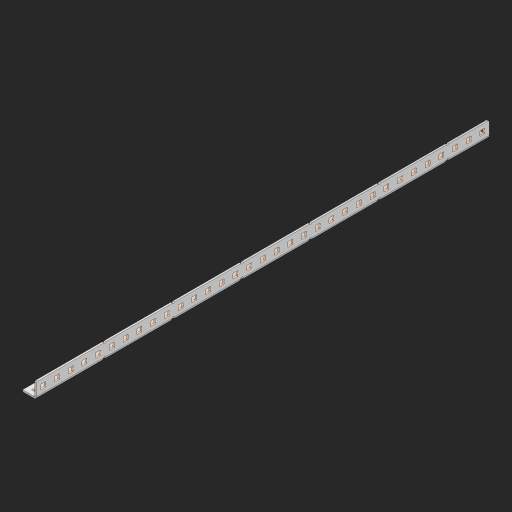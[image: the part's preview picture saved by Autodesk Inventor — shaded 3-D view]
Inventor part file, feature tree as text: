
AUTODESK INVENTOR PART (.ipt)
format: ipt  version: 2023 (Build 270158000, 158)  size: 1,024,000 bytes
history: native  units: in
note: dims shown in document units (in); Inventor stores cm internally (conversion verified against a paired STEP export)
features: other x71, extrude x65, sheet_metal_op x10, sketch x8, mirror x1, pattern_linear x1, chamfer x1
ambient origin geometry x8: Origin, YZ Plane, XZ Plane, XY Plane, X Axis, Y Axis, Z Axis, Center Point
bodies: Solid1 (feature_tree), Body (feature_tree)
feature tree (157):
  other  "Flange Pattern Plane"
  sheet_metal_op  "Flange Pattern"
  sheet_metal_op  "Body Pattern"
  other  "Arc Length"
  mirror  "Notch Mirror"
  pattern_linear  "Notch Pattern"  Spacing1=0.25in  [1 undecoded]
  chamfer  "End Chamfer"
  extrude  "Half Cut"  Depth=0.0625in
  sketch  "Sketch1"  dims[d0=1.5in]
  other  "Plate1"
  sketch  "Sketch2"  dims[d1=16.5in]
  other  "Plate2"
  sheet_metal_op  "Bend1"
  sheet_metal_op  "Corner1"
  sketch  "Sketch3"  dims[d2=0.0625in]
  other  "Flange Pattern Sketch"
  sketch  "Sketch7"  dims[d3=0.0625in]
  other  "Srf1"
  other  "Srf2"
  sketch  "Sketch8"  dims[d4=0.0312in]
  sketch  "Sketch9"  dims[d5=0.125in]
  other  "Srf91"
  sheet_metal_op  "Body Pattern Sketch"
  other  "Srf92"
  sketch  "Sketch13"  dims[d6=0.0625in]
  sketch  "Sketch14"  dims[d7=0.5in d8=90.0deg d9=0.0312in d10=0.25in d11=0.0625in d12=0.0625in d16=0.182in d17=0.02in d18=0.0625in d19=0.0in d20=0.25in d21=0.25in d46=0.172in d47=1.0in d48=0.0in d49=0.182in d50=0.02in d51=0.25in d52=0.25in d53=0.0625in d54=0.0in d55=0.172in d56=1.0in d57=0.0in d60=12.9921in d62=0.5in d63=0.3937in d65=0.5in d85=0.1473in d86=0.1782in d88=0.04in d89=0.0625in d90=0.0in d91=0.04in d92=0.0491in d95=2.5in d96=0.04in d97=0.25in d98=45.0deg d101=0.0in d102=2.497in d131=0.5in d132=12.9921in d134=0.5in d139=0.5in]
  other  "Srf856"
  other  "Srf1310"
  other  "Srf1311"
  other  "Srf1312"
  other  "Srf1376"
  other  "Srf1377"
  other  "Srf1728"
  other  "Srf1755"
  other  "Srf1878"
  other  "Srf1879"
  other  "Srf1880"
  other  "Srf1881"
  other  "Srf1882"
  other  "Srf1883"
  other  "Srf1884"
  other  "Srf1885"
  other  "Srf1886"
  other  "Srf1887"
  other  "Srf1888"
  other  "Srf1889"
  other  "Srf1890"
  other  "Srf1891"
  other  "Srf1892"
  other  "Srf1893"
  other  "Srf1894"
  other  "Srf1895"
  other  "Srf1896"
  other  "Srf1897"
  other  "Srf1898"
  other  "Srf1899"
  other  "Srf1900"
  other  "Srf1901"
  other  "Srf1902"
  other  "Srf1903"
  other  "Srf1904"
  other  "Srf1942"
  other  "Srf1943"
  other  "Srf1944"
  other  "Srf1945"
  other  "Srf1946"
  other  "Srf1947"
  other  "Srf1948"
  other  "Srf1949"
  other  "Srf1950"
  other  "Srf1951"
  other  "Srf1952"
  other  "Srf1953"
  other  "Srf1954"
  other  "Srf1955"
  other  "Srf1956"
  other  "Srf1957"
  other  "Srf1958"
  other  "Srf1959"
  other  "Srf1960"
  other  "Srf1961"
  other  "Srf1962"
  other  "Srf1963"
  other  "Srf1964"
  other  "Srf1965"
  other  "Srf1966"
  other  "Srf1967"
  other  "Srf1968"
  sheet_metal_op  "Flange Stamp"
  sheet_metal_op  "Flange Circle"
  sheet_metal_op  "Body Stamp"
  sheet_metal_op  "Body Circle"
  sheet_metal_op  "Notch"
  extrude  "ExtrusionSrf2"  Depth=0.0625in
  extrude  "ExtrusionSrf92"  Depth=0.5in
  extrude  "ExtrusionSrf856"  Depth=0.02in
  extrude  "ExtrusionSrf1310"  Depth=0.0625in
  extrude  "ExtrusionSrf1311"  TaperAngle=0.0deg  [1 undecoded]
  extrude  "ExtrusionSrf1312"  Depth=0.5in
  extrude  "ExtrusionSrf1376"  Depth=0.5in
  extrude  "ExtrusionSrf1377"  Depth=0.5in
  extrude  "ExtrusionSrf1728"  Depth=0.5in TaperAngle=0.0deg
  extrude  "ExtrusionSrf1755"  Depth=0.5in
  extrude  "ExtrusionSrf1878"  Depth=0.02in
  extrude  "ExtrusionSrf1879"  Depth=0.5in
  extrude  "ExtrusionSrf1880"  Depth=0.5in
  extrude  "ExtrusionSrf1881"  Depth=0.0625in
  extrude  "ExtrusionSrf1882"  TaperAngle=0.0deg  [1 undecoded]
  extrude  "ExtrusionSrf1883"  Depth=0.5in
  extrude  "ExtrusionSrf1884"  Depth=0.5in TaperAngle=0.0deg
  extrude  "ExtrusionSrf1885"  Depth=0.5in
  extrude  "ExtrusionSrf1886"  Depth=0.5in
  extrude  "ExtrusionSrf1887"  Depth=0.5in
  extrude  "ExtrusionSrf1888"  Depth=0.5in
  extrude  "ExtrusionSrf1889"  Depth=0.5in
  extrude  "ExtrusionSrf1890"  Depth=0.0625in
  extrude  "ExtrusionSrf1891"  TaperAngle=0.0deg  [1 undecoded]
  extrude  "ExtrusionSrf1892"  Depth=0.5in
  extrude  "ExtrusionSrf1893"  Depth=0.5in
  extrude  "ExtrusionSrf1894"  Depth=0.5in
  extrude  "ExtrusionSrf1895"  Depth=0.5in TaperAngle=45.0deg
  extrude  "ExtrusionSrf1896"  TaperAngle=0.0deg  [1 undecoded]
  extrude  "ExtrusionSrf1897"  Depth=0.5in
  extrude  "ExtrusionSrf1898"  Depth=0.5in
  extrude  "ExtrusionSrf1899"  Depth=0.5in
  extrude  "ExtrusionSrf1900"  Depth=0.5in
  extrude  "ExtrusionSrf1901"  Depth=0.5in
  extrude  "ExtrusionSrf1902"  [1 undecoded]
  extrude  "ExtrusionSrf1903"  [1 undecoded]
  extrude  "ExtrusionSrf1904"  [1 undecoded]
  extrude  "ExtrusionSrf1942"  [1 undecoded]
  extrude  "ExtrusionSrf1943"  [1 undecoded]
  extrude  "ExtrusionSrf1944"  [1 undecoded]
  extrude  "ExtrusionSrf1945"  [1 undecoded]
  extrude  "ExtrusionSrf1946"  [1 undecoded]
  extrude  "ExtrusionSrf1947"  [1 undecoded]
  extrude  "ExtrusionSrf1948"  [1 undecoded]
  extrude  "ExtrusionSrf1949"  [1 undecoded]
  extrude  "ExtrusionSrf1950"  [1 undecoded]
  extrude  "ExtrusionSrf1951"  [1 undecoded]
  extrude  "ExtrusionSrf1952"  [1 undecoded]
  extrude  "ExtrusionSrf1953"  [1 undecoded]
  extrude  "ExtrusionSrf1954"  [1 undecoded]
  extrude  "ExtrusionSrf1955"  [1 undecoded]
  extrude  "ExtrusionSrf1956"  [1 undecoded]
  extrude  "ExtrusionSrf1957"  [1 undecoded]
  extrude  "ExtrusionSrf1958"  [1 undecoded]
  extrude  "ExtrusionSrf1959"  [1 undecoded]
  extrude  "ExtrusionSrf1960"  [1 undecoded]
  extrude  "ExtrusionSrf1961"  [1 undecoded]
  extrude  "ExtrusionSrf1962"  [1 undecoded]
  extrude  "ExtrusionSrf1963"  [1 undecoded]
  extrude  "ExtrusionSrf1964"  [1 undecoded]
  extrude  "ExtrusionSrf1965"  [1 undecoded]
  extrude  "ExtrusionSrf1966"  [1 undecoded]
  extrude  "ExtrusionSrf1967"  [1 undecoded]
  extrude  "ExtrusionSrf1968"  [1 undecoded]
note: 35 required parameter values undecoded (feature->parameter linkage not recoverable at this tier; creation-order binding heuristic only, values carry confidence <= 0.55)
